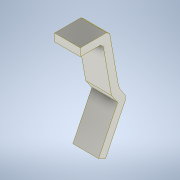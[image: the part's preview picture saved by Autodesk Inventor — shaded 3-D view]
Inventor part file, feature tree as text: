
AUTODESK INVENTOR PART (.ipt)
format: ipt  version: 2020 (Build 240168000, 168)  size: 122,880 bytes
history: native  units: mm
features: sketch x2, sweep x1, chamfer x1
ambient origin geometry x8: Origin, YZ Plane, XZ Plane, XY Plane, X Axis, Y Axis, Z Axis, Center Point
bodies: Solid1 (feature_tree)
feature tree (4):
  sweep  "Sweep1"
  chamfer  "Chamfer1"  Distance=0.4mm
  sketch  "Sketch1"  dims[d0=4.0mm d1=1.0mm]
  sketch  "Sketch2"  dims[d2=2.0mm d3=0.4mm d4=120.0deg d5=17.453293mm d6=1.0mm d7=0.3mm d8=0.0mm d9=0.0mm d10=0.1mm d11=2.0mm d12=45.0deg]
